# Revit family: Shower-Showerhead-KOHLER-Purist-K-939
name_source: partatom
category: Plumbing Fixtures
revit_build: Autodesk Revit 2015 (Build: 20140606_1530(x64)
units: mm (PartAtom-declared; Revit-internal decimal feet)

## types (7) — shared parameters
ADA Compliant = No
Assembly Code = D2010700
CW Connection = No
Date Modified = 09/18/2017
Default Elevation = 42"
Flow Rate = 2 GPM
HW Connection = Yes
Height = 3 15/16"
Inlet Connector = Inlet Connection
Length = 5 1/2"
Manufacturer = KOHLER Co.
MasterFormat 1995 = 15410
MasterFormat 2004 = 22.41.39
Material = Premium Metal Construction
Outlet Connector = Outlet Connection
Pressure = 80.00 psi
Product Documentation Link = http://www.us.kohler.com
Product Name = Purist
Product Page URL = http://www.us.kohler.com
URL = http://www.us.kohler.com
Vent Connection = No
Waste Connection = No
Width = 5 1/2"

## per-type parameters (varying)
| type | Description | Finish | Model | Type |
| 2.0 gpm Showerhead-CP-Polished Chrome | 2.0 gpm single-function showerhead with Katalyst air-induction spray | Metal-Kohler-CP-Polished Chrome | K-939-CP | 1 |
| 2.0 gpm Showerhead-BN-Vibrant Brushed Nickel | 2.0 gpm single-function showerhead with Katalyst air-induction spray | Metal-Kohler-BN-Vibrant Brushed Nickel | K-939-BN | 2 |
| 2.0 gpm Showerhead-BV-Vibrant Brushed Bronze | 2.0 gpm single-function showerhead with Katalyst air-induction spray | Metal-Kohler-BV-Vibrant Brushed Bronze | K-939-BV | 3 |
| 2.0 gpm Showerhead-RGD-Vibrant Rose Gold | 2.0 gpm single-function showerhead with Katalyst air-induction spray | Kohler-Metal-RGD-Polished_Rose_Gold | K-939-RGD | 4 |
| 2.0 gpm Showerhead-TT-Vibrant Titanium | 2.0 gpm single-function showerhead with Katalyst air-induction spray | Metal-Kohler-TT-Vibrant Titanium | K-939-TT | 5 |
| 2.0 gpm Showerhead-SN-Vibrant Polished Nickel | 2.0 gpm single-function showerhead with Katalyst air-induction spray | Kohler-Metal-SN-Vibrant_Polished_Nickel | K-939-SN | 6 |
| 1.75 gpm Showerhead-CP-Polished Chrome | 1.75 gpm single-function showerhead with Katalyst air-induction spray | Metal-Kohler-CP-Polished Chrome | K-939-G-CP | 7 |

## geometry (parser evidence)
native form markers: Blend x2, Sweep x4
no freeform markers — native parametric forms only
